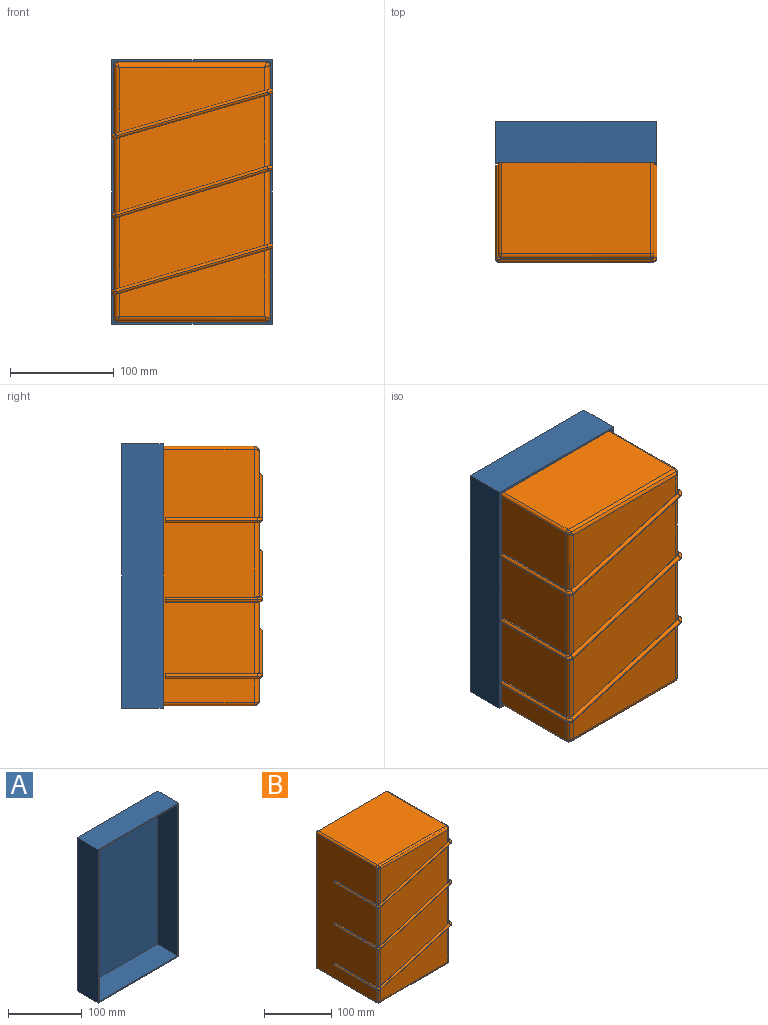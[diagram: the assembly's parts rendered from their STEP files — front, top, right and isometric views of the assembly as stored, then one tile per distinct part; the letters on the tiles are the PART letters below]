
ASSEMBLY  parts=2 mates=1
PART A: 11 faces, bbox 155x40x255 mm
  f0: plane 255x155mm, normal (0,-1,0), area 1624mm2, adj f1,f2,f3,f4,f6,f7,f8,f9
  f1: plane 155x40mm, normal (0,0,1), area 6200mm2, adj f0,f2,f4,f5
  f2: plane 255x40mm, normal (-1,0,0), area 10200mm2, adj f0,f1,f3,f5
  f3: plane 155x40mm, normal (0,0,-1), area 6200mm2, adj f0,f2,f4,f5
  f4: plane 255x40mm, normal (1,0,0), area 10200mm2, adj f0,f1,f3,f5
  f5: plane 255x155mm, normal (0,1,0), area 39525mm2, adj f1,f2,f3,f4
  f6: plane 151x39mm, normal (0,0,-1), area 5889mm2, adj f0,f7,f9,f10
  f7: plane 251x39mm, normal (1,0,0), area 9789mm2, adj f0,f6,f8,f10
  f8: plane 151x39mm, normal (0,0,1), area 5889mm2, adj f0,f7,f9,f10
  f9: plane 251x39mm, normal (-1,0,0), area 9789mm2, adj f0,f6,f8,f10
  f10: plane 251x151mm, normal (0,-1,0), area 37901mm2, adj f6,f7,f8,f9
PART B: 74 faces, bbox 156.6x133.7x250.6 mm
  f0: plane 250x150mm, normal (0,1,0), area 1576.3mm2, adj f19,f20,f21,f22,f29,f31,f33,f35
  f1: plane 151.6x91.9mm, normal (0.28,0,-0.96), area 198.3mm2, adj f5,f13,f14,f15,f22,f40,f42,f44
  f2: plane 151.64x91.94mm, normal (0.29,0,-0.96), area 203.2mm2, adj f7,f10,f11,f12,f22,f48,f50,f52
  f3: plane 151.62x91.92mm, normal (0.28,0,-0.96), area 200.1mm2, adj f9,f22,f23,f25,f26,f56,f58,f60
  f4: cylinder r=2.5mm len=88.8mm, axis (0,1,0), area 384.9mm2, adj f5,f18,f22,f36,f45,f70
  f5: cylinder r=2.5mm len=88.8mm, axis (0,1,0), area 277.9mm2, adj f1,f4,f46,f70
  f6: cylinder r=2.5mm len=88.8mm, axis (0,1,0), area 383.8mm2, adj f7,f15,f22,f37,f53,f69
  f7: cylinder r=2.5mm len=88.8mm, axis (0,1,0), area 272.7mm2, adj f2,f6,f54,f69
  f8: cylinder r=2.5mm len=88.8mm, axis (0,1,0), area 384.5mm2, adj f9,f12,f22,f38,f61,f68
  f9: cylinder r=2.5mm len=88.8mm, axis (0,1,0), area 276mm2, adj f3,f8,f62,f68
  f10: plane 140x111.66mm, normal (0,-1,0), area 9761.7mm2, adj f2,f11,f12,f38
  f11: cylinder r=5mm len=70.34mm, axis (0,0,1), area 539.8mm2, adj f2,f10,f20,f38,f48
  f12: cylinder r=5mm len=72.11mm, axis (0,0,-1), area 553.8mm2, adj f2,f8,f10,f22,f38
  f13: plane 140x111.49mm, normal (0,-1,0), area 9806.8mm2, adj f1,f14,f15,f37
  f14: cylinder r=5mm len=72.92mm, axis (0,0,1), area 560.3mm2, adj f1,f13,f20,f37,f40
  f15: cylinder r=5mm len=70.13mm, axis (0,0,-1), area 538.3mm2, adj f1,f6,f13,f22,f37
  f16: plane 140x62.38mm, normal (0,-1,0), area 5927.2mm2, adj f17,f18,f24,f36
  f17: cylinder r=5mm len=65.82mm, axis (0,0,1), area 503.4mm2, adj f16,f20,f28,f36
  f18: cylinder r=5mm len=24.29mm, axis (0,0,-1), area 176.5mm2, adj f4,f16,f22,f30,f36
  f19: plane 144x125mm, normal (0,0,1), area 18000mm2, adj f0,f24,f29,f31
  f20: plane 244x125mm, normal (-1,0,0), area 29215.5mm2, adj f0,f11,f14,f17,f25,f29,f33,f36
  f21: plane 144x125mm, normal (0,0,-1), area 18000mm2, adj f0,f27,f33,f35
  f22: plane 244x125mm, normal (1,0,0), area 29215.5mm2, adj f0,f1,f2,f3,f4,f6,f8,f12
  f23: plane 140x63.43mm, normal (0,-1,0), area 6004.2mm2, adj f3,f25,f26,f27
  f24: cylinder r=5mm len=144mm, axis (1,0,0), area 1115.3mm2, adj f16,f19,f28,f30
  f25: cylinder r=5mm len=24.35mm, axis (0,0,1), area 176.8mm2, adj f3,f20,f23,f32,f56
  f26: cylinder r=5mm len=66.89mm, axis (0,0,-1), area 511.8mm2, adj f3,f22,f23,f34
  f27: cylinder r=5mm len=144mm, axis (-1,0,0), area 1115.3mm2, adj f21,f23,f32,f34
  f28: bspline ~5.26x5mm, area 16.3mm2, adj f17,f24,f29
  f29: cylinder r=3mm len=125mm, axis (0,-1,0), area 589mm2, adj f0,f19,f20,f28
  f30: bspline ~6.03x5mm, area 16.3mm2, adj f18,f24,f31
  f31: cylinder r=3mm len=125mm, axis (0,1,0), area 589mm2, adj f0,f19,f22,f30
  f32: bspline ~5.26x5mm, area 16.3mm2, adj f25,f27,f33
  f33: cylinder r=3mm len=125mm, axis (0,1,0), area 589mm2, adj f0,f20,f21,f32
  f34: bspline ~6.03x5mm, area 16.3mm2, adj f26,f27,f35
  f35: cylinder r=3mm len=125mm, axis (0,-1,0), area 589mm2, adj f0,f21,f22,f34
  f36: plane 151.6x91.9mm, normal (-0.28,0,0.96), area 198.3mm2, adj f4,f16,f17,f18,f20,f39,f41,f43
  f37: plane 151.64x91.94mm, normal (-0.29,0,0.96), area 203.2mm2, adj f6,f13,f14,f15,f20,f47,f49,f51
  f38: plane 151.62x91.92mm, normal (-0.28,0,0.96), area 200.1mm2, adj f8,f10,f11,f12,f20,f55,f57,f59
  f39: cylinder r=2.5mm len=88.8mm, axis (0,1,0), area 277.9mm2, adj f36,f40,f41,f73
  f40: cylinder r=2.5mm len=88.8mm, axis (0,1,0), area 384.9mm2, adj f1,f14,f20,f39,f42,f73
  f41: bspline ~5.92x5.87mm, area 21.3mm2, adj f36,f39,f42,f43
  f42: bspline ~6.51x5.31mm, area 28.2mm2, adj f1,f40,f41,f43,f44
  f43: cylinder r=2.5mm len=146.66mm, axis (0.96,0,0.28), area 581.7mm2, adj f36,f41,f42,f44,f45
  f44: cylinder r=2.5mm len=146.66mm, axis (-0.96,0,-0.28), area 581.7mm2, adj f1,f42,f43,f45,f46
  f45: bspline ~6.51x5.31mm, area 28.2mm2, adj f4,f36,f43,f44,f46
  f46: bspline ~5.92x5.87mm, area 21.3mm2, adj f1,f5,f44,f45
  f47: cylinder r=2.5mm len=88.8mm, axis (0,1,0), area 272.7mm2, adj f37,f48,f49,f72
  f48: cylinder r=2.5mm len=88.8mm, axis (0,1,0), area 383.8mm2, adj f2,f11,f20,f47,f50,f72
  f49: bspline ~5.9x5.22mm, area 21mm2, adj f37,f47,f50,f51
  f50: bspline ~6.55x5.32mm, area 28.4mm2, adj f2,f48,f49,f51,f52
  f51: cylinder r=2.5mm len=146.7mm, axis (0.96,0,0.29), area 582.8mm2, adj f37,f49,f50,f52,f53
  f52: cylinder r=2.5mm len=146.7mm, axis (-0.96,0,-0.29), area 582.8mm2, adj f2,f50,f51,f53,f54
  f53: bspline ~6.55x5.32mm, area 28.4mm2, adj f6,f37,f51,f52,f54
  f54: bspline ~5.93x5.87mm, area 21mm2, adj f2,f7,f52,f53
  f55: cylinder r=2.5mm len=88.8mm, axis (0,1,0), area 276mm2, adj f38,f56,f57,f71
  f56: cylinder r=2.5mm len=88.8mm, axis (0,1,0), area 384.5mm2, adj f3,f20,f25,f55,f58,f71
  f57: bspline ~5.92x5.87mm, area 21.2mm2, adj f38,f55,f58,f59
  f58: bspline ~6.52x5.31mm, area 28.3mm2, adj f3,f56,f57,f59,f60
  f59: cylinder r=2.5mm len=146.68mm, axis (0.96,0,0.28), area 582.1mm2, adj f38,f57,f58,f60,f61
  f60: cylinder r=2.5mm len=146.68mm, axis (-0.96,0,-0.28), area 582.1mm2, adj f3,f58,f59,f61,f62
  f61: bspline ~6.52x5.31mm, area 28.3mm2, adj f8,f38,f59,f60,f62
  f62: bspline ~5.92x5.87mm, area 21.2mm2, adj f3,f9,f60,f61
  f63: plane 246x128mm, normal (-1,0,0), area 31488mm2, adj f0,f64,f66,f67
  f64: plane 146x128mm, normal (0,0,-1), area 18688mm2, adj f0,f63,f65,f67
  f65: plane 246x128mm, normal (1,0,0), area 31488mm2, adj f0,f64,f66,f67
  f66: plane 146x128mm, normal (0,0,1), area 18688mm2, adj f0,f63,f65,f67
  f67: plane 246x146mm, normal (0,1,0), area 35916mm2, adj f63,f64,f65,f66
  f68: plane 5.04x3mm, normal (0,1,0), area 11.8mm2, adj f3,f8,f9,f22
  f69: plane 5.04x3mm, normal (0,1,0), area 11.7mm2, adj f2,f6,f7,f22
  f70: plane 5.04x3mm, normal (0,1,0), area 11.8mm2, adj f1,f4,f5,f22
  f71: plane 5.04x3mm, normal (0,1,0), area 11.8mm2, adj f20,f38,f55,f56
  f72: plane 5.04x3mm, normal (0,1,0), area 11.7mm2, adj f20,f37,f47,f48
  f73: plane 5.04x3mm, normal (0,1,0), area 11.8mm2, adj f20,f36,f39,f40
PLACE A t=(-187.05,42.87,-64.1)mm
PLACE B t=(-187.05,80.05,-64.1)mm
MATE slider B.f0 <-> A.f10  axis (0,1,0) through (-187.05,80.05,-64.1)mm
